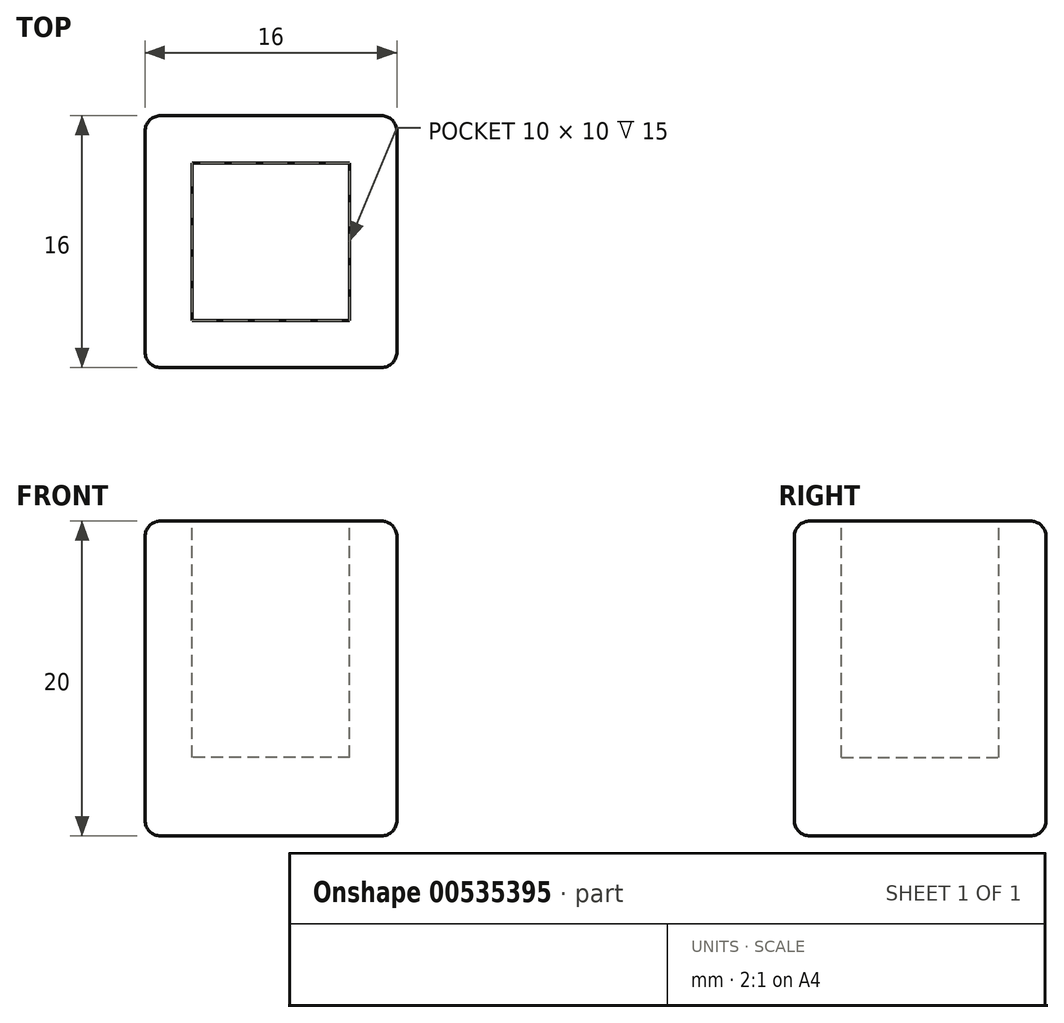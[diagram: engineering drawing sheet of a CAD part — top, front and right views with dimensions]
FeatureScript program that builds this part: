
annotation { "Feature Type Name" : "Feature", "Feature Type Description" : "" }
export const myFeature = defineFeature(function(context is Context, id is Id, definition is map)
    precondition{}
    {
        {
            var Q0;
            Q0=qCreatedBy(makeId("Top.planeOp"),FACE);
            var sketch = newSketch(context, id + "F0", { "sketchPlane" : qUnion([Q0])});
            skLineSegment(sketch, "E0.bottom", {"start": v(-61.23, 6.02) * mm, "end": v(-45.23, 6.02) * mm});
            skLineSegment(sketch, "E0.top", {"start": v(-61.23, -9.98) * mm, "end": v(-45.23, -9.98) * mm});
            skLineSegment(sketch, "E0.left", {"start": v(-61.23, 6.02) * mm, "end": v(-61.23, -9.98) * mm});
            skLineSegment(sketch, "E0.right", {"start": v(-45.23, 6.02) * mm, "end": v(-45.23, -9.98) * mm});
            skSolve(sketch);
        }
        {
            var Q0;
            Q0=qSketchRegion(id+"F0",true);
            extrude(context, id + "F1", {"entities" : qUnion([Q0]), "depth" : 20 * mm});
        }
        {
            var Q0;
            Q0=makeQuery(id+"F1.opExtrude","CAP_FACE",FACE,{"disambiguationData":[OSD([sQuery(id+"F0.wireOp",EDGE,"E0.bottom"),sQuery(id+"F0.wireOp",EDGE,"E0.top"),sQuery(id+"F0.wireOp",EDGE,"E0.left"),sQuery(id+"F0.wireOp",EDGE,"E0.right")])],"isStart":false});
            var sketch = newSketch(context, id + "F2", { "sketchPlane" : qUnion([Q0])});
            skLineSegment(sketch, "E1.bottom", {"start": v(-61.23, 6.02) * mm, "end": v(-48.23, 6.02) * mm, "construction": true});
            skLineSegment(sketch, "E1.top", {"start": v(-61.23, -6.98) * mm, "end": v(-48.23, -6.98) * mm, "construction": true});
            skLineSegment(sketch, "E1.left", {"start": v(-61.23, 6.02) * mm, "end": v(-61.23, -6.98) * mm, "construction": true});
            skLineSegment(sketch, "E1.right", {"start": v(-48.23, 6.02) * mm, "end": v(-48.23, -6.98) * mm, "construction": true});
            skLineSegment(sketch, "E2.bottom", {"start": v(-48.23, -6.98) * mm, "end": v(-58.23, -6.98) * mm});
            skLineSegment(sketch, "E2.top", {"start": v(-48.23, 3.02) * mm, "end": v(-58.23, 3.02) * mm});
            skLineSegment(sketch, "E2.left", {"start": v(-48.23, -6.98) * mm, "end": v(-48.23, 3.02) * mm});
            skLineSegment(sketch, "E2.right", {"start": v(-58.23, -6.98) * mm, "end": v(-58.23, 3.02) * mm});
            skSolve(sketch);
        }
        {
            var Q0;
            Q0=qSketchRegion(id+"F2",true);
            extrude(context, id + "F3", {"entities" : qUnion([Q0]), "operationType" : NewBodyOperationType.REMOVE, "oppositeDirection" : true, "depth" : 15 * mm});
        }
        {
            var Q0;
            Q0=makeQuery(id+"F1.opExtrude","SWEPT_FACE",FACE,{"disambiguationData":[OSD([sQuery(id+"F0.wireOp",EDGE,"E0.right")])]});
            var Q1;
            Q1=makeQuery(id+"F1.opExtrude","SWEPT_FACE",FACE,{"disambiguationData":[OSD([sQuery(id+"F0.wireOp",EDGE,"E0.top")])]});
            var Q2;
            Q2=makeQuery(id+"F1.opExtrude","SWEPT_FACE",FACE,{"disambiguationData":[OSD([sQuery(id+"F0.wireOp",EDGE,"E0.left")])]});
            var Q3;
            Q3=makeQuery(id+"F1.opExtrude","SWEPT_FACE",FACE,{"disambiguationData":[OSD([sQuery(id+"F0.wireOp",EDGE,"E0.bottom")])]});
            fillet(context, id + "F4", {"entities" : qUnion([Q0, Q1, Q2, Q3]), "radius" : 1 * mm, "tangentPropagation" : true, "allowEdgeOverflow" : false});
        }
    });
